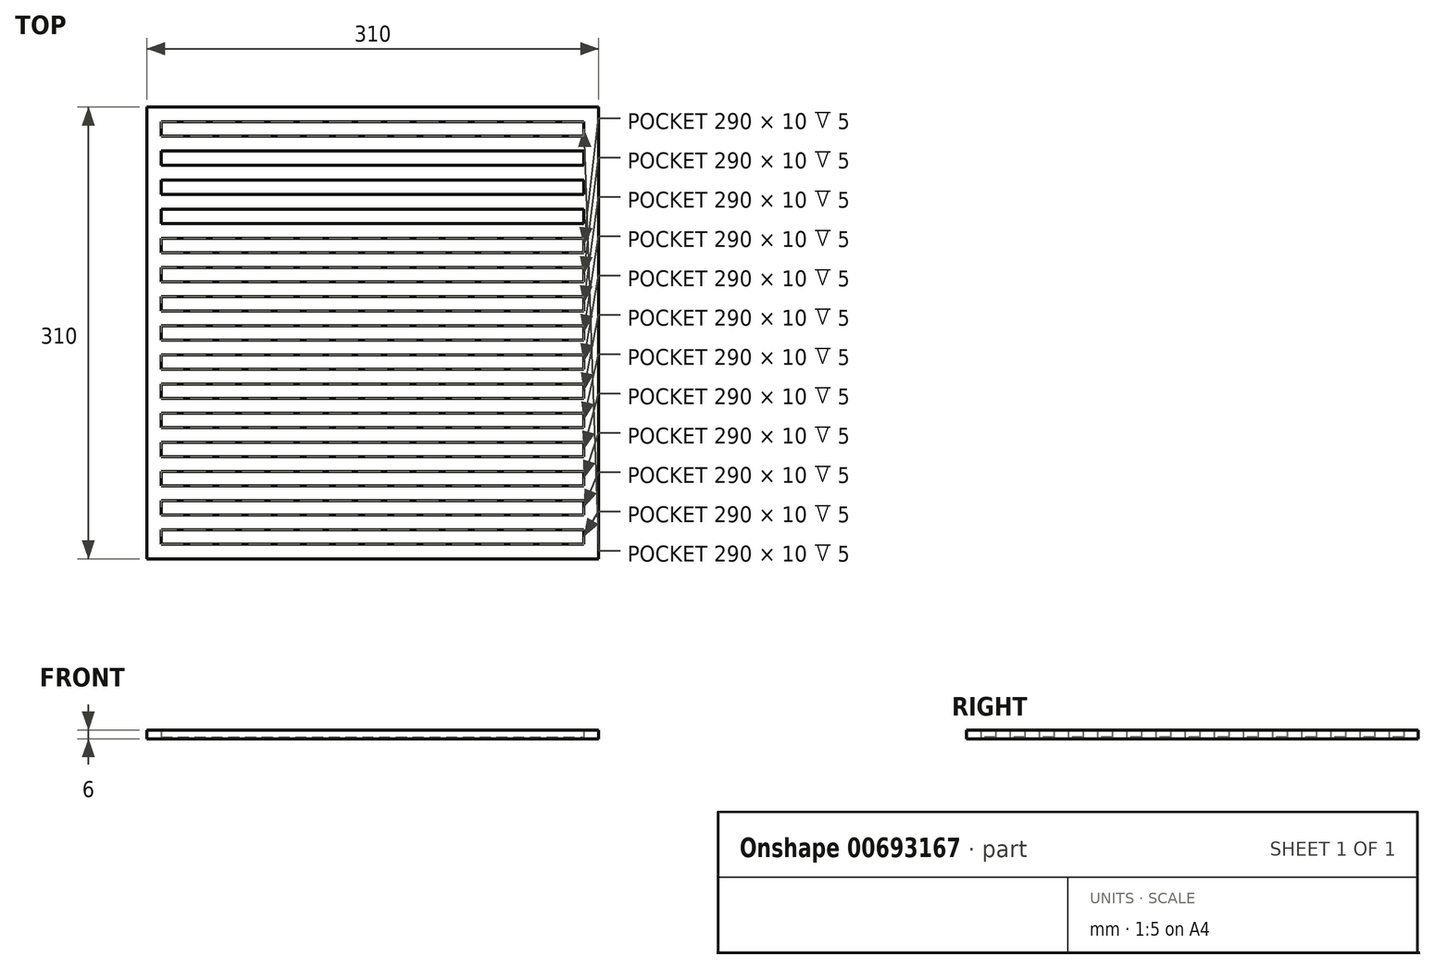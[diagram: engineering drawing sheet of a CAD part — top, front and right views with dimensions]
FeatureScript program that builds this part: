
annotation { "Feature Type Name" : "Feature", "Feature Type Description" : "" }
export const myFeature = defineFeature(function(context is Context, id is Id, definition is map)
    precondition{}
    {
        {
            var Q0;
            Q0=qCreatedBy(makeId("Top.planeOp"),FACE);
            var sketch = newSketch(context, id + "F0", { "sketchPlane" : qUnion([Q0])});
            skLineSegment(sketch, "E0.bottom", {"start": v(-278.38, -4.15) * mm, "end": v(31.62, -4.15) * mm});
            skLineSegment(sketch, "E0.top", {"start": v(-278.38, -314.15) * mm, "end": v(31.62, -314.15) * mm});
            skLineSegment(sketch, "E0.left", {"start": v(-278.38, -4.15) * mm, "end": v(-278.38, -314.15) * mm});
            skLineSegment(sketch, "E0.right", {"start": v(31.62, -4.15) * mm, "end": v(31.62, -314.15) * mm});
            skLineSegment(sketch, "E1.bottom", {"start": v(-268.38, -14.15) * mm, "end": v(21.62, -14.15) * mm});
            skLineSegment(sketch, "E1.top", {"start": v(-268.38, -24.15) * mm, "end": v(21.62, -24.15) * mm});
            skLineSegment(sketch, "E1.left", {"start": v(-268.38, -14.15) * mm, "end": v(-268.38, -24.15) * mm});
            skLineSegment(sketch, "E1.right", {"start": v(21.62, -14.15) * mm, "end": v(21.62, -24.15) * mm});
            skLineSegment(sketch, "E2.0.1.0", {"start": v(21.62, -34.15) * mm, "end": v(21.62, -44.15) * mm});
            skLineSegment(sketch, "E2.0.1.1", {"start": v(-268.38, -34.15) * mm, "end": v(21.62, -34.15) * mm});
            skLineSegment(sketch, "E2.0.1.2", {"start": v(-268.38, -44.15) * mm, "end": v(21.62, -44.15) * mm});
            skLineSegment(sketch, "E2.0.1.3", {"start": v(-268.38, -34.15) * mm, "end": v(-268.38, -44.15) * mm});
            skLineSegment(sketch, "E2.0.2.0", {"start": v(21.62, -54.15) * mm, "end": v(21.62, -64.15) * mm});
            skLineSegment(sketch, "E2.0.2.1", {"start": v(-268.38, -54.15) * mm, "end": v(21.62, -54.15) * mm});
            skLineSegment(sketch, "E2.0.2.2", {"start": v(-268.38, -64.15) * mm, "end": v(21.62, -64.15) * mm});
            skLineSegment(sketch, "E2.0.2.3", {"start": v(-268.38, -54.15) * mm, "end": v(-268.38, -64.15) * mm});
            skLineSegment(sketch, "E2.0.3.0", {"start": v(21.62, -74.15) * mm, "end": v(21.62, -84.15) * mm});
            skLineSegment(sketch, "E2.0.3.1", {"start": v(-268.38, -74.15) * mm, "end": v(21.62, -74.15) * mm});
            skLineSegment(sketch, "E2.0.3.2", {"start": v(-268.38, -84.15) * mm, "end": v(21.62, -84.15) * mm});
            skLineSegment(sketch, "E2.0.3.3", {"start": v(-268.38, -74.15) * mm, "end": v(-268.38, -84.15) * mm});
            skLineSegment(sketch, "E2.0.4.0", {"start": v(21.62, -94.15) * mm, "end": v(21.62, -104.15) * mm});
            skLineSegment(sketch, "E2.0.4.1", {"start": v(-268.38, -94.15) * mm, "end": v(21.62, -94.15) * mm});
            skLineSegment(sketch, "E2.0.4.2", {"start": v(-268.38, -104.15) * mm, "end": v(21.62, -104.15) * mm});
            skLineSegment(sketch, "E2.0.4.3", {"start": v(-268.38, -94.15) * mm, "end": v(-268.38, -104.15) * mm});
            skLineSegment(sketch, "E2.0.5.0", {"start": v(21.62, -114.15) * mm, "end": v(21.62, -124.15) * mm});
            skLineSegment(sketch, "E2.0.5.1", {"start": v(-268.38, -114.15) * mm, "end": v(21.62, -114.15) * mm});
            skLineSegment(sketch, "E2.0.5.2", {"start": v(-268.38, -124.15) * mm, "end": v(21.62, -124.15) * mm});
            skLineSegment(sketch, "E2.0.5.3", {"start": v(-268.38, -114.15) * mm, "end": v(-268.38, -124.15) * mm});
            skLineSegment(sketch, "E2.0.6.0", {"start": v(21.62, -134.15) * mm, "end": v(21.62, -144.15) * mm});
            skLineSegment(sketch, "E2.0.6.1", {"start": v(-268.38, -134.15) * mm, "end": v(21.62, -134.15) * mm});
            skLineSegment(sketch, "E2.0.6.2", {"start": v(-268.38, -144.15) * mm, "end": v(21.62, -144.15) * mm});
            skLineSegment(sketch, "E2.0.6.3", {"start": v(-268.38, -134.15) * mm, "end": v(-268.38, -144.15) * mm});
            skLineSegment(sketch, "E2.direction1", {"start": v(21.62, -24.15) * mm, "end": v(325.03, -24.15) * mm, "construction": true});
            skLineSegment(sketch, "E2.direction2", {"start": v(21.62, -24.15) * mm, "end": v(21.62, -44.15) * mm, "construction": true});
            skLineSegment(sketch, "E3.0.0.7", {"start": v(21.62, -154.15) * mm, "end": v(21.62, -164.15) * mm});
            skLineSegment(sketch, "E3.3.0.7", {"start": v(-268.38, -154.15) * mm, "end": v(21.62, -154.15) * mm});
            skLineSegment(sketch, "E3.6.0.7", {"start": v(-268.38, -164.15) * mm, "end": v(21.62, -164.15) * mm});
            skLineSegment(sketch, "E3.9.0.7", {"start": v(-268.38, -154.15) * mm, "end": v(-268.38, -164.15) * mm});
            skLineSegment(sketch, "E3.0.0.8", {"start": v(21.62, -174.15) * mm, "end": v(21.62, -184.15) * mm});
            skLineSegment(sketch, "E3.3.0.8", {"start": v(-268.38, -174.15) * mm, "end": v(21.62, -174.15) * mm});
            skLineSegment(sketch, "E3.6.0.8", {"start": v(-268.38, -184.15) * mm, "end": v(21.62, -184.15) * mm});
            skLineSegment(sketch, "E3.9.0.8", {"start": v(-268.38, -174.15) * mm, "end": v(-268.38, -184.15) * mm});
            skLineSegment(sketch, "E3.0.0.9", {"start": v(21.62, -194.15) * mm, "end": v(21.62, -204.15) * mm});
            skLineSegment(sketch, "E3.3.0.9", {"start": v(-268.38, -194.15) * mm, "end": v(21.62, -194.15) * mm});
            skLineSegment(sketch, "E3.6.0.9", {"start": v(-268.38, -204.15) * mm, "end": v(21.62, -204.15) * mm});
            skLineSegment(sketch, "E3.9.0.9", {"start": v(-268.38, -194.15) * mm, "end": v(-268.38, -204.15) * mm});
            skLineSegment(sketch, "E3.0.0.10", {"start": v(21.62, -214.15) * mm, "end": v(21.62, -224.15) * mm});
            skLineSegment(sketch, "E3.3.0.10", {"start": v(-268.38, -214.15) * mm, "end": v(21.62, -214.15) * mm});
            skLineSegment(sketch, "E3.6.0.10", {"start": v(-268.38, -224.15) * mm, "end": v(21.62, -224.15) * mm});
            skLineSegment(sketch, "E3.9.0.10", {"start": v(-268.38, -214.15) * mm, "end": v(-268.38, -224.15) * mm});
            skLineSegment(sketch, "E3.0.0.11", {"start": v(21.62, -234.15) * mm, "end": v(21.62, -244.15) * mm});
            skLineSegment(sketch, "E3.3.0.11", {"start": v(-268.38, -234.15) * mm, "end": v(21.62, -234.15) * mm});
            skLineSegment(sketch, "E3.6.0.11", {"start": v(-268.38, -244.15) * mm, "end": v(21.62, -244.15) * mm});
            skLineSegment(sketch, "E3.9.0.11", {"start": v(-268.38, -234.15) * mm, "end": v(-268.38, -244.15) * mm});
            skLineSegment(sketch, "E3.0.0.12", {"start": v(21.62, -254.15) * mm, "end": v(21.62, -264.15) * mm});
            skLineSegment(sketch, "E3.3.0.12", {"start": v(-268.38, -254.15) * mm, "end": v(21.62, -254.15) * mm});
            skLineSegment(sketch, "E3.6.0.12", {"start": v(-268.38, -264.15) * mm, "end": v(21.62, -264.15) * mm});
            skLineSegment(sketch, "E3.9.0.12", {"start": v(-268.38, -254.15) * mm, "end": v(-268.38, -264.15) * mm});
            skLineSegment(sketch, "E3.0.0.13", {"start": v(21.62, -274.15) * mm, "end": v(21.62, -284.15) * mm});
            skLineSegment(sketch, "E3.3.0.13", {"start": v(-268.38, -274.15) * mm, "end": v(21.62, -274.15) * mm});
            skLineSegment(sketch, "E3.6.0.13", {"start": v(-268.38, -284.15) * mm, "end": v(21.62, -284.15) * mm});
            skLineSegment(sketch, "E3.9.0.13", {"start": v(-268.38, -274.15) * mm, "end": v(-268.38, -284.15) * mm});
            skLineSegment(sketch, "E4.0.0.14", {"start": v(21.62, -294.15) * mm, "end": v(21.62, -304.15) * mm});
            skLineSegment(sketch, "E4.3.0.14", {"start": v(-268.38, -294.15) * mm, "end": v(21.62, -294.15) * mm});
            skLineSegment(sketch, "E4.6.0.14", {"start": v(-268.38, -304.15) * mm, "end": v(21.62, -304.15) * mm});
            skLineSegment(sketch, "E4.9.0.14", {"start": v(-268.38, -294.15) * mm, "end": v(-268.38, -304.15) * mm});
            skSolve(sketch);
        }
        {
            var Q0;
            Q0=qSketchRegion(id+"F0",true);
            extrude(context, id + "F1", {"entities" : qUnion([Q0]), "depth" : 5 * mm, "offsetDistance" : 25 * mm});
        }
        {
            var Q0;
            Q0=makeQuery(id+"F1.opExtrude","CAP_FACE",FACE,{"disambiguationData":[OSD([sQuery(id+"F0.wireOp",EDGE,"E0.bottom"),sQuery(id+"F0.wireOp",EDGE,"E0.top"),sQuery(id+"F0.wireOp",EDGE,"E0.left"),sQuery(id+"F0.wireOp",EDGE,"E0.right"),sQuery(id+"F0.wireOp",EDGE,"E1.bottom"),sQuery(id+"F0.wireOp",EDGE,"E1.top"),sQuery(id+"F0.wireOp",EDGE,"E1.left"),sQuery(id+"F0.wireOp",EDGE,"E1.right"),sQuery(id+"F0.wireOp",EDGE,"E2.0.1.0"),sQuery(id+"F0.wireOp",EDGE,"E2.0.1.1"),sQuery(id+"F0.wireOp",EDGE,"E2.0.1.2"),sQuery(id+"F0.wireOp",EDGE,"E2.0.1.3"),sQuery(id+"F0.wireOp",EDGE,"E2.0.2.0"),sQuery(id+"F0.wireOp",EDGE,"E2.0.2.1"),sQuery(id+"F0.wireOp",EDGE,"E2.0.2.2"),sQuery(id+"F0.wireOp",EDGE,"E2.0.2.3"),sQuery(id+"F0.wireOp",EDGE,"E2.0.3.0"),sQuery(id+"F0.wireOp",EDGE,"E2.0.3.1"),sQuery(id+"F0.wireOp",EDGE,"E2.0.3.2"),sQuery(id+"F0.wireOp",EDGE,"E2.0.3.3"),sQuery(id+"F0.wireOp",EDGE,"E2.0.4.0"),sQuery(id+"F0.wireOp",EDGE,"E2.0.4.1"),sQuery(id+"F0.wireOp",EDGE,"E2.0.4.2"),sQuery(id+"F0.wireOp",EDGE,"E2.0.4.3"),sQuery(id+"F0.wireOp",EDGE,"E2.0.5.0"),sQuery(id+"F0.wireOp",EDGE,"E2.0.5.1"),sQuery(id+"F0.wireOp",EDGE,"E2.0.5.2"),sQuery(id+"F0.wireOp",EDGE,"E2.0.5.3"),sQuery(id+"F0.wireOp",EDGE,"E2.0.6.0"),sQuery(id+"F0.wireOp",EDGE,"E2.0.6.1"),sQuery(id+"F0.wireOp",EDGE,"E2.0.6.2"),sQuery(id+"F0.wireOp",EDGE,"E2.0.6.3")])],"isStart":true});
            var sketch = newSketch(context, id + "F2", { "sketchPlane" : qUnion([Q0])});
            skLineSegment(sketch, "E5.bottom", {"start": v(-278.38, 4.15) * mm, "end": v(31.62, 4.15) * mm});
            skLineSegment(sketch, "E5.top", {"start": v(-278.38, 314.15) * mm, "end": v(31.62, 314.15) * mm});
            skLineSegment(sketch, "E5.left", {"start": v(-278.38, 4.15) * mm, "end": v(-278.38, 314.15) * mm});
            skLineSegment(sketch, "E5.right", {"start": v(31.62, 4.15) * mm, "end": v(31.62, 314.15) * mm});
            skSolve(sketch);
        }
        {
            var Q0;
            Q0=qSketchRegion(id+"F2",true);
            extrude(context, id + "F3", {"entities" : qUnion([Q0]), "operationType" : NewBodyOperationType.ADD, "depth" : 1 * mm, "offsetDistance" : 25 * mm});
        }
    });
